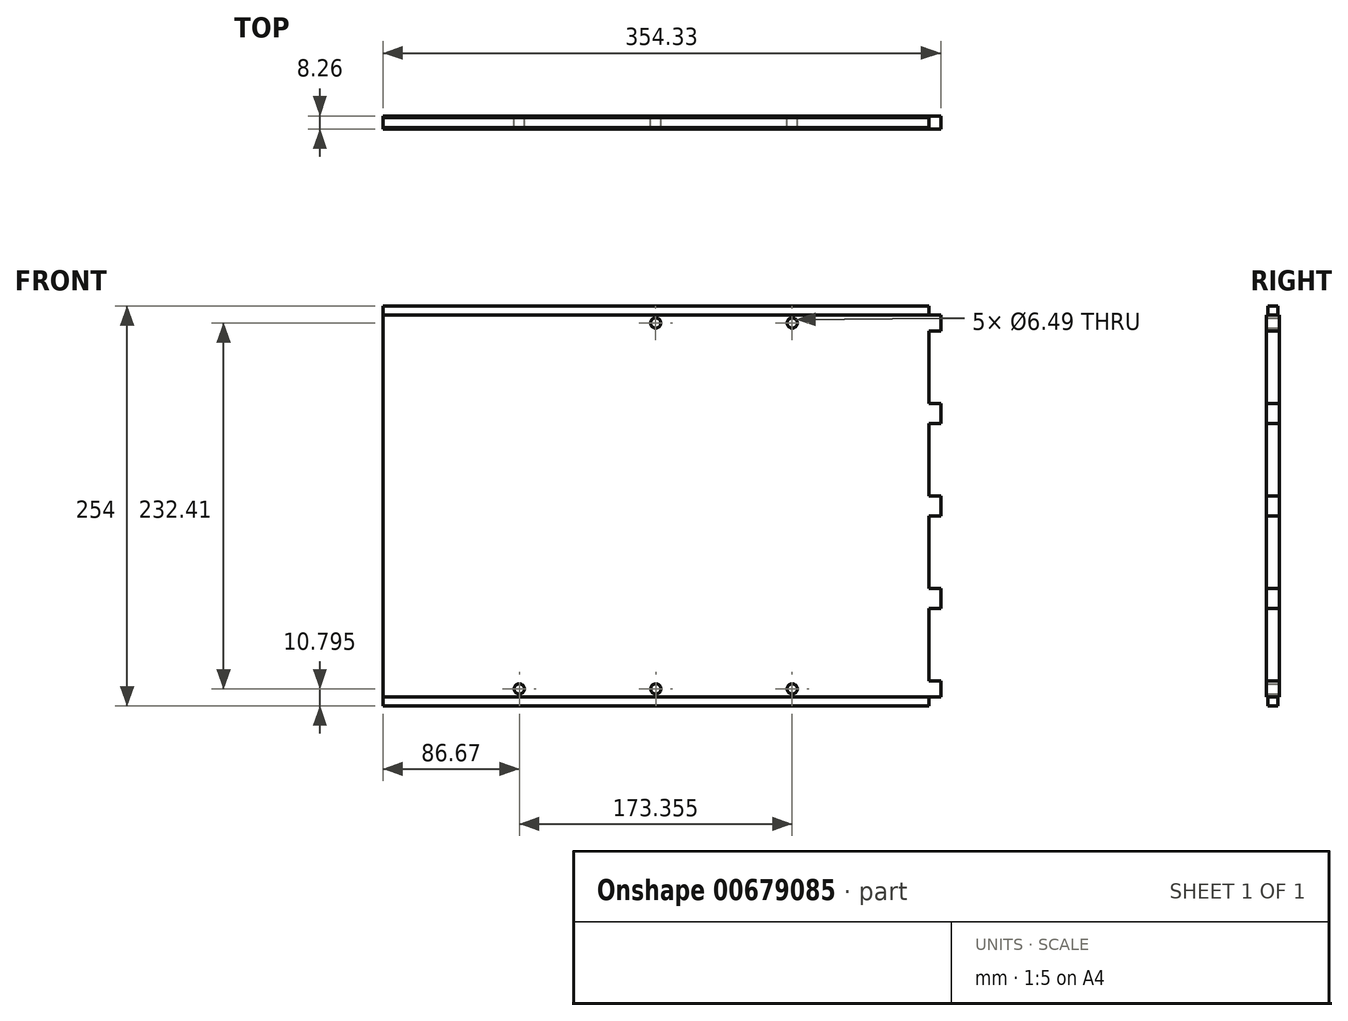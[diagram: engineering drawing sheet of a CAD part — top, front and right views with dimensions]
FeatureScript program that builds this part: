
annotation { "Feature Type Name" : "Feature", "Feature Type Description" : "" }
export const myFeature = defineFeature(function(context is Context, id is Id, definition is map)
    precondition{}
    {
        {
            var Q0;
            Q0=qCreatedBy(makeId("Front.planeOp"),FACE);
            var sketch = newSketch(context, id + "F0", { "sketchPlane" : qUnion([Q0])});
            skLineSegment(sketch, "E0.bottom", {"start": v(-173.36, 127) * mm, "end": v(173.35, 127) * mm});
            skLineSegment(sketch, "E0.top", {"start": v(-173.35, -127) * mm, "end": v(173.36, -127) * mm});
            skLineSegment(sketch, "E0.left", {"start": v(-173.36, 127) * mm, "end": v(-173.35, -127) * mm});
            skLineSegment(sketch, "E0.right", {"start": v(173.35, 127) * mm, "end": v(173.36, -127) * mm});
            skPoint(sketch, "E0.middle", {"position": v(0, 0) * mm});
            skLineSegment(sketch, "E1.bottom", {"start": v(-173.35, 121.29) * mm, "end": v(173.35, 121.29) * mm});
            skLineSegment(sketch, "E1.top", {"start": v(-173.36, -121.28) * mm, "end": v(173.36, -121.28) * mm});
            skLineSegment(sketch, "E1.left", {"start": v(-173.35, 121.29) * mm, "end": v(-173.36, -121.28) * mm});
            skLineSegment(sketch, "E1.right", {"start": v(173.36, 121.29) * mm, "end": v(173.35, -121.28) * mm});
            skLineSegment(sketch, "E2.bottom", {"start": v(173.36, -121.28) * mm, "end": v(180.97, -121.28) * mm});
            skLineSegment(sketch, "E2.top", {"start": v(173.35, -111.12) * mm, "end": v(180.97, -111.12) * mm});
            skLineSegment(sketch, "E2.left", {"start": v(173.35, -121.28) * mm, "end": v(173.35, -111.12) * mm});
            skLineSegment(sketch, "E2.right", {"start": v(180.97, -121.28) * mm, "end": v(180.97, -111.12) * mm});
            skLineSegment(sketch, "E3.bottom", {"start": v(173.36, -65.09) * mm, "end": v(180.97, -65.09) * mm});
            skLineSegment(sketch, "E3.top", {"start": v(173.36, -52.39) * mm, "end": v(180.97, -52.39) * mm});
            skLineSegment(sketch, "E3.left", {"start": v(173.36, -65.09) * mm, "end": v(173.36, -52.39) * mm});
            skLineSegment(sketch, "E3.right", {"start": v(180.97, -65.09) * mm, "end": v(180.97, -52.39) * mm});
            skLineSegment(sketch, "E4.bottom", {"start": v(173.36, -6.35) * mm, "end": v(180.97, -6.35) * mm});
            skLineSegment(sketch, "E4.top", {"start": v(173.36, 6.35) * mm, "end": v(180.97, 6.35) * mm});
            skLineSegment(sketch, "E4.left", {"start": v(173.36, -6.35) * mm, "end": v(173.36, 6.35) * mm});
            skLineSegment(sketch, "E4.right", {"start": v(180.97, -6.35) * mm, "end": v(180.97, 6.35) * mm});
            skLineSegment(sketch, "E5.bottom", {"start": v(173.35, 52.39) * mm, "end": v(180.97, 52.39) * mm});
            skLineSegment(sketch, "E5.top", {"start": v(173.35, 65.09) * mm, "end": v(180.97, 65.09) * mm});
            skLineSegment(sketch, "E5.left", {"start": v(173.36, 52.39) * mm, "end": v(173.36, 65.09) * mm});
            skLineSegment(sketch, "E5.right", {"start": v(180.97, 52.39) * mm, "end": v(180.97, 65.09) * mm});
            skLineSegment(sketch, "E6.bottom", {"start": v(173.36, 121.29) * mm, "end": v(180.97, 121.29) * mm});
            skLineSegment(sketch, "E6.top", {"start": v(173.36, 111.13) * mm, "end": v(180.97, 111.13) * mm});
            skLineSegment(sketch, "E6.left", {"start": v(173.36, 121.29) * mm, "end": v(173.36, 111.13) * mm});
            skLineSegment(sketch, "E6.right", {"start": v(180.97, 121.29) * mm, "end": v(180.97, 111.13) * mm});
            skCircle(sketch, "E7", {"center": v(0, -116.2) * mm, "radius": 3.25 * mm});
            skPoint(sketch, "E7.centerSnap0", {"position": v(0, -121.28) * mm});
            skCircle(sketch, "E8", {"center": v(86.66, -116.2) * mm, "radius": 3.25 * mm});
            skCircle(sketch, "E9", {"center": v(-86.7, -116.2) * mm, "radius": 3.25 * mm});
            skCircle(sketch, "E10", {"center": v(-0.03, 116.2) * mm, "radius": 3.25 * mm});
            skCircle(sketch, "E11", {"center": v(86.66, 116.2) * mm, "radius": 3.25 * mm});
            skPoint(sketch, "E12.middle", {"position": v(-116.2, 0) * mm});
            skSolve(sketch);
        }
        {
            var Q0;
            Q0=makeQuery(id+"F0.imprint","IMPRINT",FACE,{"disambiguationData":[TD([[makeQuery(id+"F0.imprint","IMPRINT",EDGE,{"derivedFrom":sQuery(id+"F0.wireOp",EDGE,"E1.bottom")}),-1.0]])]});
            var Q1;
            Q1=makeQuery(id+"F0.imprint","IMPRINT",FACE,{"disambiguationData":[TD([[makeQuery(id+"F0.imprint","IMPRINT",EDGE,{"derivedFrom":sQuery(id+"F0.wireOp",EDGE,"E6.bottom")}),-1.0]])]});
            var Q2;
            Q2=makeQuery(id+"F0.imprint","IMPRINT",FACE,{"disambiguationData":[TD([[makeQuery(id+"F0.imprint","IMPRINT",EDGE,{"derivedFrom":sQuery(id+"F0.wireOp",EDGE,"E5.bottom")}),1.0]])]});
            var Q3;
            Q3=makeQuery(id+"F0.imprint","IMPRINT",FACE,{"disambiguationData":[TD([[makeQuery(id+"F0.imprint","IMPRINT",EDGE,{"derivedFrom":sQuery(id+"F0.wireOp",EDGE,"E4.bottom")}),1.0]])]});
            var Q4;
            Q4=makeQuery(id+"F0.imprint","IMPRINT",FACE,{"disambiguationData":[TD([[makeQuery(id+"F0.imprint","IMPRINT",EDGE,{"derivedFrom":sQuery(id+"F0.wireOp",EDGE,"E3.bottom")}),1.0]])]});
            var Q5;
            Q5=makeQuery(id+"F0.imprint","IMPRINT",FACE,{"disambiguationData":[TD([[makeQuery(id+"F0.imprint","IMPRINT",EDGE,{"derivedFrom":sQuery(id+"F0.wireOp",EDGE,"E2.bottom")}),1.0]])]});
            extrude(context, id + "F1", {"entities" : qUnion([Q0, Q1, Q2, Q3, Q4, Q5]), "endBound" : BoundingType.SYMMETRIC, "depth" : 8.25 * mm, "offsetDistance" : 25.4 * mm});
        }
        {
            var Q0;
            {var subQ0=sQuery(id+"F0.wireOp",EDGE,"E0.bottom");Q0=makeQuery(id+"F0.imprint","IMPRINT",FACE,{"disambiguationData":[TD([[makeQuery(id+"F0.imprint","IMPRINT",EDGE,{"derivedFrom":subQ0}),-1.0]])]});}
            var Q1;
            {var subQ0=sQuery(id+"F0.wireOp",EDGE,"E0.top");Q1=makeQuery(id+"F0.imprint","IMPRINT",FACE,{"disambiguationData":[TD([[makeQuery(id+"F0.imprint","IMPRINT",EDGE,{"derivedFrom":subQ0}),1.0]])]});}
            extrude(context, id + "F2", {"entities" : qUnion([Q0, Q1]), "operationType" : NewBodyOperationType.ADD, "endBound" : BoundingType.SYMMETRIC, "depth" : 6.35 * mm, "offsetDistance" : 25.4 * mm});
        }
    });
